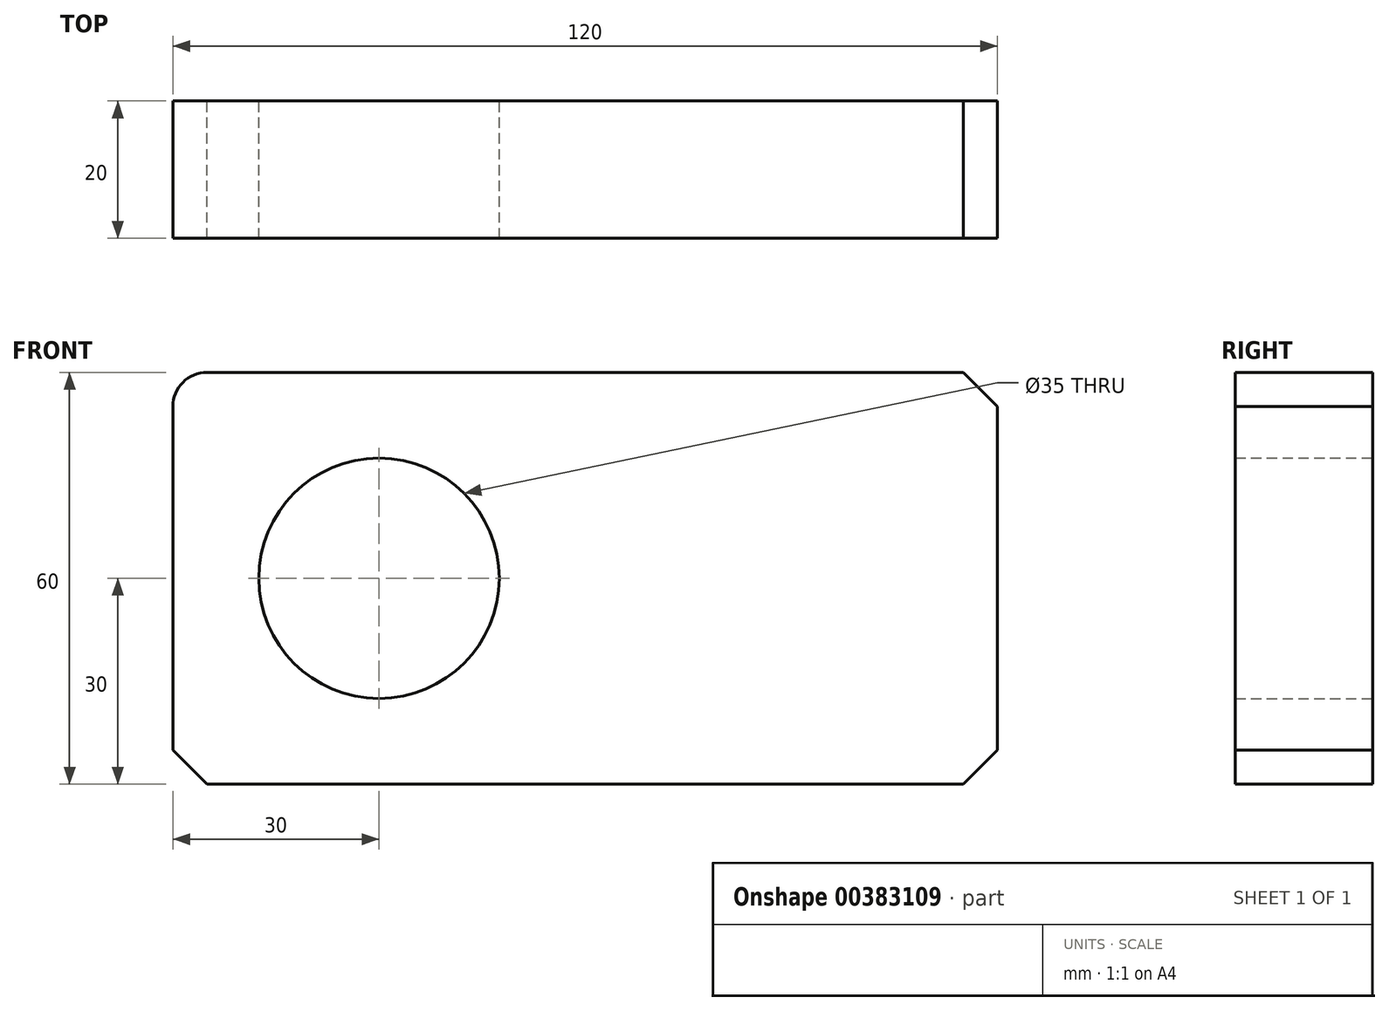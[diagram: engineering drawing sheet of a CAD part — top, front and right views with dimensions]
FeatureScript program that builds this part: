
annotation { "Feature Type Name" : "Feature", "Feature Type Description" : "" }
export const myFeature = defineFeature(function(context is Context, id is Id, definition is map)
    precondition{}
    {
        {
            var Q0;
            Q0=qCreatedBy(makeId("Front.planeOp"),FACE);
            var sketch = newSketch(context, id + "F0", { "sketchPlane" : qUnion([Q0]), "disableImprinting" : false});
            skLineSegment(sketch, "E0.bottom", {"start": v(0, 0) * mm, "end": v(120, 0) * mm});
            skLineSegment(sketch, "E0.top", {"start": v(0, 60) * mm, "end": v(120, 60) * mm});
            skLineSegment(sketch, "E0.left", {"start": v(0, 0) * mm, "end": v(0, 60) * mm});
            skLineSegment(sketch, "E0.right", {"start": v(120, 0) * mm, "end": v(120, 60) * mm});
            skCircle(sketch, "E1", {"center": v(30, 30) * mm, "radius": 17.5 * mm});
            skSolve(sketch);
        }
        {
            var Q0;
            Q0 = qSketchRegion(id + "F0ElxvRm8Ro4iJu_0", true);
            var Q1;
            Q1=makeQuery(id+"F0.imprint","IMPRINT",FACE,{"disambiguationData":[TD([[makeQuery(id+"F0.imprint","IMPRINT",EDGE,{"derivedFrom":sQuery(id+"F0.wireOp",EDGE,"E0.bottom")}),1.0]])]});
            extrude(context, id + "F1", {"entities" : qUnion([Q0, Q1]), "depth" : 20 * mm});
        }
        {
            var Q0;
            Q0=makeQuery(id+"F1.opExtrude","SWEPT_EDGE",EDGE,{"disambiguationData":[OSD([sQuery(id+"F0.wireOp",EDGE,"E0.top"),sQuery(id+"F0.wireOp",EDGE,"E0.left")])]});
            fillet(context, id + "F2", {"entities" : qUnion([Q0]), "radius" : 5 * mm, "tangentPropagation" : true, "allowEdgeOverflow" : false});
        }
        {
            var Q0;
            Q0=makeQuery(id+"F1.opExtrude","SWEPT_EDGE",EDGE,{"disambiguationData":[OSD([sQuery(id+"F0.wireOp",EDGE,"E0.top"),sQuery(id+"F0.wireOp",EDGE,"E0.right")])]});
            var Q1;
            Q1=makeQuery(id+"F1.opExtrude","SWEPT_EDGE",EDGE,{"disambiguationData":[OSD([sQuery(id+"F0.wireOp",EDGE,"E0.bottom"),sQuery(id+"F0.wireOp",EDGE,"E0.left")])]});
            var Q2;
            Q2=makeQuery(id+"F1.opExtrude","SWEPT_EDGE",EDGE,{"disambiguationData":[OSD([sQuery(id+"F0.wireOp",EDGE,"E0.bottom"),sQuery(id+"F0.wireOp",EDGE,"E0.right")])]});
            chamfer(context, id + "F3", {"entities" : qUnion([Q0, Q1, Q2]), "width" : 5 * mm, "tangentPropagation" : true});
        }
        {
            var Q0;
            Q0=makeQuery(id+"F1.opExtrude","SWEPT_FACE",FACE,{"disambiguationData":[OSD([sQuery(id+"F0.wireOp",EDGE,"E0.right")])]});
            cPlane(context, id + "F4", {"entities" : qUnion([Q0]), "cplaneType" : CPlaneType.OFFSET, "offset" : 30 * mm, "oppositeDirection" : true, "width" : 150 * mm, "height" : 150 * mm});
        }
    });
